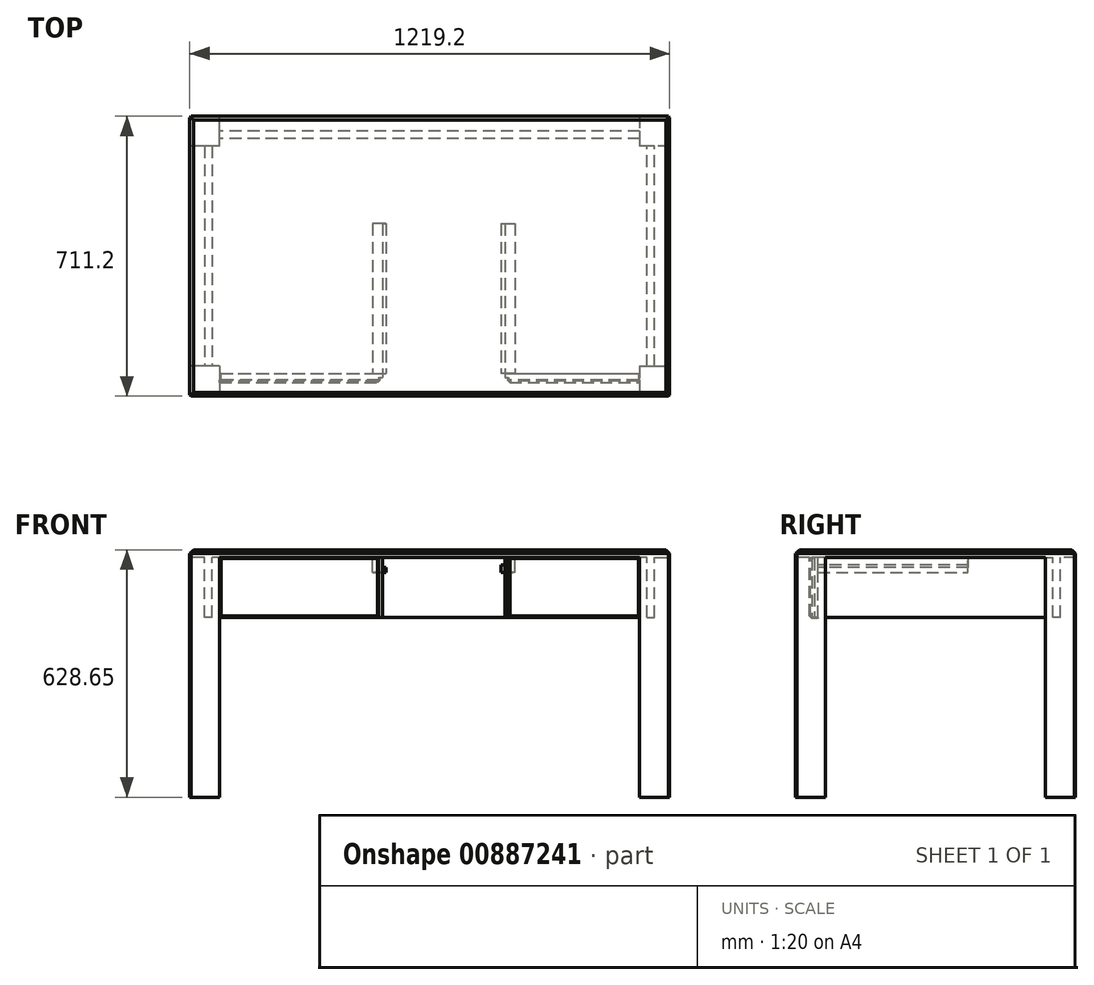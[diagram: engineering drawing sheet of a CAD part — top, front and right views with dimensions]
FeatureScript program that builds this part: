
annotation { "Feature Type Name" : "Feature", "Feature Type Description" : "" }
export const myFeature = defineFeature(function(context is Context, id is Id, definition is map)
    precondition{}
    {
        {
            var Q0;
            Q0=qCreatedBy(makeId("Top.planeOp"),FACE);
            var sketch = newSketch(context, id + "F0", { "sketchPlane" : qUnion([Q0])});
            skLineSegment(sketch, "E0.bottom", {"start": v(609.6, 355.6) * mm, "end": v(-609.6, 355.6) * mm});
            skLineSegment(sketch, "E0.top", {"start": v(609.6, -355.6) * mm, "end": v(-609.6, -355.6) * mm});
            skLineSegment(sketch, "E0.left", {"start": v(609.6, 355.6) * mm, "end": v(609.6, -355.6) * mm});
            skLineSegment(sketch, "E0.right", {"start": v(-609.6, 355.6) * mm, "end": v(-609.6, -355.6) * mm});
            skPoint(sketch, "E0.middle", {"position": v(0, 0) * mm});
            skSolve(sketch);
        }
        {
            var Q0;
            Q0 = qSketchRegion(id + "F0", true);
            extrude(context, id + "F1", {"entities" : qUnion([Q0]), "depth" : 19.05 * mm, "offsetDistance" : 25.4 * mm});
        }
        {
            var Q0;
            Q0=makeQuery(id+"F1.opExtrude","CAP_FACE",FACE,{"disambiguationData":[OSD([sQuery(id+"F0.wireOp",EDGE,"E0.bottom"),sQuery(id+"F0.wireOp",EDGE,"E0.top"),sQuery(id+"F0.wireOp",EDGE,"E0.left"),sQuery(id+"F0.wireOp",EDGE,"E0.right")])],"isStart":true});
            var sketch = newSketch(context, id + "F2", { "sketchPlane" : qUnion([Q0])});
            skLineSegment(sketch, "E1.bottom", {"start": v(-533.4, 279.4) * mm, "end": v(-609.6, 279.4) * mm});
            skLineSegment(sketch, "E1.top", {"start": v(-533.4, 355.6) * mm, "end": v(-609.6, 355.6) * mm});
            skLineSegment(sketch, "E1.left", {"start": v(-533.4, 279.4) * mm, "end": v(-533.4, 355.6) * mm});
            skLineSegment(sketch, "E1.right", {"start": v(-609.6, 279.4) * mm, "end": v(-609.6, 355.6) * mm});
            skSolve(sketch);
        }
        {
            var Q0;
            Q0 = qSketchRegion(id + "F2", true);
            extrude(context, id + "F3", {"entities" : qUnion([Q0]), "operationType" : NewBodyOperationType.ADD, "depth" : 609.6 * mm, "offsetDistance" : 25.4 * mm});
        }
        {
            var Q0;
            Q0=makeQuery(id+"F1.opExtrude","CAP_FACE",FACE,{"disambiguationData":[OSD([sQuery(id+"F0.wireOp",EDGE,"E0.bottom"),sQuery(id+"F0.wireOp",EDGE,"E0.top"),sQuery(id+"F0.wireOp",EDGE,"E0.left"),sQuery(id+"F0.wireOp",EDGE,"E0.right")])],"isStart":true});
            var sketch = newSketch(context, id + "F4", { "sketchPlane" : qUnion([Q0])});
            skLineSegment(sketch, "E2.bottom", {"start": v(533.4, 279.4) * mm, "end": v(609.6, 279.4) * mm});
            skLineSegment(sketch, "E2.top", {"start": v(533.4, 355.6) * mm, "end": v(609.6, 355.6) * mm});
            skLineSegment(sketch, "E2.left", {"start": v(533.4, 279.4) * mm, "end": v(533.4, 355.6) * mm});
            skLineSegment(sketch, "E2.right", {"start": v(609.6, 279.4) * mm, "end": v(609.6, 355.6) * mm});
            skLineSegment(sketch, "E3.bottom", {"start": v(609.6, -355.6) * mm, "end": v(533.4, -355.6) * mm});
            skLineSegment(sketch, "E3.top", {"start": v(609.6, -279.4) * mm, "end": v(533.4, -279.4) * mm});
            skLineSegment(sketch, "E3.left", {"start": v(609.6, -355.6) * mm, "end": v(609.6, -279.4) * mm});
            skLineSegment(sketch, "E3.right", {"start": v(533.4, -355.6) * mm, "end": v(533.4, -279.4) * mm});
            skLineSegment(sketch, "E4.bottom", {"start": v(-533.4, -279.4) * mm, "end": v(-609.6, -279.4) * mm});
            skLineSegment(sketch, "E4.top", {"start": v(-533.4, -355.6) * mm, "end": v(-609.6, -355.6) * mm});
            skLineSegment(sketch, "E4.left", {"start": v(-533.4, -279.4) * mm, "end": v(-533.4, -355.6) * mm});
            skLineSegment(sketch, "E4.right", {"start": v(-609.6, -279.4) * mm, "end": v(-609.6, -355.6) * mm});
            skSolve(sketch);
        }
        {
            var Q0;
            Q0 = qSketchRegion(id + "F4", true);
            extrude(context, id + "F5", {"entities" : qUnion([Q0]), "operationType" : NewBodyOperationType.ADD, "depth" : 609.6 * mm, "offsetDistance" : 25.4 * mm});
        }
        {
            var Q0;
            Q0=makeQuery(id+"F1.opExtrude","CAP_FACE",FACE,{"disambiguationData":[OSD([sQuery(id+"F0.wireOp",EDGE,"E0.bottom"),sQuery(id+"F0.wireOp",EDGE,"E0.top"),sQuery(id+"F0.wireOp",EDGE,"E0.left"),sQuery(id+"F0.wireOp",EDGE,"E0.right")])],"isStart":true});
            var sketch = newSketch(context, id + "F6", { "sketchPlane" : qUnion([Q0])});
            skLineSegment(sketch, "E5", {"start": v(-533.4, 317.5) * mm, "end": v(533.4, 317.5) * mm});
            skLineSegment(sketch, "E6", {"start": v(571.5, 279.4) * mm, "end": v(571.5, -279.4) * mm});
            skLineSegment(sketch, "E7", {"start": v(533.4, -317.5) * mm, "end": v(-533.4, -317.5) * mm});
            skLineSegment(sketch, "E8", {"start": v(-571.5, -279.4) * mm, "end": v(-571.5, 279.4) * mm});
            skLineSegment(sketch, "E9.0", {"start": v(-552.45, -279.4) * mm, "end": v(-552.45, 279.4) * mm});
            skLineSegment(sketch, "E10.0", {"start": v(-533.4, 298.45) * mm, "end": v(533.4, 298.45) * mm});
            skLineSegment(sketch, "E11.0", {"start": v(552.45, 279.4) * mm, "end": v(552.45, -279.4) * mm});
            skLineSegment(sketch, "E12.0", {"start": v(533.4, -298.45) * mm, "end": v(-533.4, -298.45) * mm});
            skSolve(sketch);
        }
        {
            var Q0;
            {var subQ0=sQuery(id+"F6.wireOp",EDGE,"E8");Q0=makeQuery(id+"F6.imprint","IMPRINT",FACE,{"disambiguationData":[TD([[makeQuery(id+"F6.imprint","IMPRINT",EDGE,{"derivedFrom":subQ0}),-1.0]])]});}
            var Q1;
            {var subQ0=sQuery(id+"F6.wireOp",EDGE,"E5");Q1=makeQuery(id+"F6.imprint","IMPRINT",FACE,{"disambiguationData":[TD([[makeQuery(id+"F6.imprint","IMPRINT",EDGE,{"derivedFrom":subQ0}),-1.0]])]});}
            var Q2;
            {var subQ0=sQuery(id+"F6.wireOp",EDGE,"E6");Q2=makeQuery(id+"F6.imprint","IMPRINT",FACE,{"disambiguationData":[TD([[makeQuery(id+"F6.imprint","IMPRINT",EDGE,{"derivedFrom":subQ0}),-1.0]])]});}
            var Q3;
            {var subQ0=sQuery(id+"F6.wireOp",EDGE,"E7");Q3=makeQuery(id+"F6.imprint","IMPRINT",FACE,{"disambiguationData":[TD([[makeQuery(id+"F6.imprint","IMPRINT",EDGE,{"derivedFrom":subQ0}),-1.0]])]});}
            extrude(context, id + "F7", {"entities" : qUnion([Q0, Q1, Q2, Q3]), "operationType" : NewBodyOperationType.ADD, "depth" : 152.4 * mm, "offsetDistance" : 25.4 * mm});
        }
        {
            var Q0;
            Q0=makeQuery(id+"F7.opExtrude","SWEPT_FACE",FACE,{"disambiguationData":[OSD([sQuery(id+"F6.wireOp",EDGE,"E5")])]});
            var sketch = newSketch(context, id + "F8", { "sketchPlane" : qUnion([Q0])});
            skLineSegment(sketch, "E13", {"start": v(-129.98, 0) * mm, "end": v(-129.98, -152.4) * mm});
            skLineSegment(sketch, "E14", {"start": v(-129.98, -152.4) * mm, "end": v(200.22, -152.4) * mm});
            skLineSegment(sketch, "E15", {"start": v(200.22, -152.4) * mm, "end": v(200.22, 0) * mm});
            skLineSegment(sketch, "E16", {"start": v(200.22, 0) * mm, "end": v(-129.98, 0) * mm});
            skLineSegment(sketch, "E17", {"start": v(-120.46, 0) * mm, "end": v(-120.46, -152.4) * mm});
            skLineSegment(sketch, "E18", {"start": v(-120.46, -152.4) * mm, "end": v(190.7, -152.4) * mm});
            skLineSegment(sketch, "E19", {"start": v(190.7, -152.4) * mm, "end": v(190.7, 0) * mm});
            skLineSegment(sketch, "E20", {"start": v(190.7, 0) * mm, "end": v(-120.46, 0) * mm});
            skSolve(sketch);
        }
        {
            var Q0;
            Q0 = qSketchRegion(id + "F8", true);
            extrude(context, id + "F9", {"entities" : qUnion([Q0]), "operationType" : NewBodyOperationType.REMOVE, "oppositeDirection" : true, "depth" : 9.52 * mm, "offsetDistance" : 25.4 * mm});
        }
        {
            var Q0;
            Q0=makeQuery(id+"F8.imprint","IMPRINT",FACE,{"disambiguationData":[TD([[makeQuery(id+"F8.imprint","IMPRINT",EDGE,{"derivedFrom":sQuery(id+"F8.wireOp",EDGE,"E17")}),1.0]])]});
            extrude(context, id + "F10", {"entities" : qUnion([Q0]), "operationType" : NewBodyOperationType.REMOVE, "oppositeDirection" : true, "depth" : 119.56 * mm, "offsetDistance" : 25.4 * mm});
        }
        {
            var Q0;
            {var subQ0=sQuery(id+"F8.wireOp",EDGE,"E20");var subQ2=sQuery(id+"F0.wireOp",EDGE,"E0.top");var subQ4=makeQuery(id+"F1.opExtrude","CAP_FACE",FACE,{"disambiguationData":[OSD([sQuery(id+"F0.wireOp",EDGE,"E0.bottom"),subQ2,sQuery(id+"F0.wireOp",EDGE,"E0.left"),sQuery(id+"F0.wireOp",EDGE,"E0.right")])],"isStart":true});Q0=makeQuery(id+"F10.boolean.opBoolean","MERGE",FACE,{"derivedFrom":[makeQuery(id+"F7.boolean.opBoolean","SPLIT",FACE,{"disambiguationData":[TD([makeQuery(id+"F7.opExtrude","SWEPT_FACE",FACE,{"disambiguationData":[OSD([sQuery(id+"F6.wireOp",EDGE,"E9.0")])]})])],"derivedFrom":subQ4}),makeQuery(id+"F9.boolean.opBoolean","MERGE",FACE,{"derivedFrom":[makeQuery(id+"F7.boolean.opBoolean","SPLIT",FACE,{"disambiguationData":[TD([makeQuery(id+"F1.opExtrude","SWEPT_FACE",FACE,{"disambiguationData":[OSD([subQ2])]})])],"derivedFrom":subQ4})],"fromTools":[makeQuery(id+"F9.opExtrude","SWEPT_FACE",FACE,{"disambiguationData":[OSD([sQuery(id+"F8.wireOp",EDGE,"E16"),subQ0])]})]})],"fromTools":[makeQuery(id+"F10.opExtrude","SWEPT_FACE",FACE,{"disambiguationData":[OSD([subQ0])]})]});}
            var sketch = newSketch(context, id + "F11", { "sketchPlane" : qUnion([Q0])});
            skLineSegment(sketch, "E21", {"start": v(-120.46, 298.45) * mm, "end": v(-120.46, -82.55) * mm});
            skLineSegment(sketch, "E22", {"start": v(-120.46, -82.55) * mm, "end": v(-145.86, -82.55) * mm});
            skLineSegment(sketch, "E23", {"start": v(-145.86, -82.55) * mm, "end": v(-145.86, 298.45) * mm});
            skLineSegment(sketch, "E24", {"start": v(190.7, 298.45) * mm, "end": v(190.7, -82.55) * mm});
            skLineSegment(sketch, "E25", {"start": v(190.7, -82.55) * mm, "end": v(216.1, -82.55) * mm});
            skLineSegment(sketch, "E26", {"start": v(216.1, -82.55) * mm, "end": v(216.1, 298.45) * mm});
            skLineSegment(sketch, "E27", {"start": v(-120.46, 298.45) * mm, "end": v(-110.93, 298.45) * mm});
            skLineSegment(sketch, "E28", {"start": v(-110.93, 298.45) * mm, "end": v(-110.93, -82.55) * mm});
            skLineSegment(sketch, "E29", {"start": v(-110.93, -82.55) * mm, "end": v(-120.46, -82.55) * mm});
            skLineSegment(sketch, "E30", {"start": v(190.7, 298.45) * mm, "end": v(181.17, 298.45) * mm});
            skLineSegment(sketch, "E31", {"start": v(181.17, 298.45) * mm, "end": v(181.17, -82.55) * mm});
            skLineSegment(sketch, "E32", {"start": v(181.17, -82.55) * mm, "end": v(190.7, -82.55) * mm});
            skSolve(sketch);
        }
        {
            var Q0;
            {var subQ0=sQuery(id+"F11.wireOp",EDGE,"E21");Q0=makeQuery(id+"F11.imprint","IMPRINT",FACE,{"disambiguationData":[TD([[makeQuery(id+"F11.imprint","IMPRINT",EDGE,{"derivedFrom":subQ0}),-1.0]])]});}
            var Q1;
            Q1 = qSketchRegion(id + "F11", true);
            var Q2;
            {var subQ0=sQuery(id+"F11.wireOp",EDGE,"E24");Q2=makeQuery(id+"F11.imprint","IMPRINT",FACE,{"disambiguationData":[TD([[makeQuery(id+"F11.imprint","IMPRINT",EDGE,{"derivedFrom":subQ0}),1.0]])]});}
            extrude(context, id + "F12", {"entities" : qUnion([Q0, Q1, Q2]), "operationType" : NewBodyOperationType.ADD, "depth" : 38.1 * mm, "offsetDistance" : 25.4 * mm});
        }
        {
            var Q0;
            Q0=makeQuery(id+"F3.boolean.opBoolean","MERGE",EDGE,{"derivedFrom":[makeQuery(id+"F1.opExtrude","SWEPT_EDGE",EDGE,{"disambiguationData":[OSD([sQuery(id+"F0.wireOp",EDGE,"E0.top"),sQuery(id+"F0.wireOp",EDGE,"E0.right")])]}),makeQuery(id+"F3.opExtrude","SWEPT_EDGE",EDGE,{"disambiguationData":[OSD([sQuery(id+"F2.wireOp",EDGE,"E1.top"),sQuery(id+"F2.wireOp",EDGE,"E1.right")])]})]});
            var Q1;
            Q1=makeQuery(id+"F5.boolean.opBoolean","MERGE",EDGE,{"derivedFrom":[makeQuery(id+"F1.opExtrude","SWEPT_EDGE",EDGE,{"disambiguationData":[OSD([sQuery(id+"F0.wireOp",EDGE,"E0.bottom"),sQuery(id+"F0.wireOp",EDGE,"E0.right")])]}),makeQuery(id+"F5.opExtrude","SWEPT_EDGE",EDGE,{"disambiguationData":[OSD([sQuery(id+"F4.wireOp",EDGE,"E4.top"),sQuery(id+"F4.wireOp",EDGE,"E4.right")])]})]});
            var Q2;
            Q2=makeQuery(id+"F5.boolean.opBoolean","MERGE",EDGE,{"derivedFrom":[makeQuery(id+"F1.opExtrude","SWEPT_EDGE",EDGE,{"disambiguationData":[OSD([sQuery(id+"F0.wireOp",EDGE,"E0.bottom"),sQuery(id+"F0.wireOp",EDGE,"E0.left")])]}),makeQuery(id+"F5.opExtrude","SWEPT_EDGE",EDGE,{"disambiguationData":[OSD([sQuery(id+"F4.wireOp",EDGE,"E3.bottom"),sQuery(id+"F4.wireOp",EDGE,"E3.left")])]})]});
            var Q3;
            Q3=makeQuery(id+"F5.boolean.opBoolean","MERGE",EDGE,{"derivedFrom":[makeQuery(id+"F1.opExtrude","SWEPT_EDGE",EDGE,{"disambiguationData":[OSD([sQuery(id+"F0.wireOp",EDGE,"E0.top"),sQuery(id+"F0.wireOp",EDGE,"E0.left")])]}),makeQuery(id+"F5.opExtrude","SWEPT_EDGE",EDGE,{"disambiguationData":[OSD([sQuery(id+"F4.wireOp",EDGE,"E2.top"),sQuery(id+"F4.wireOp",EDGE,"E2.right")])]})]});
            var Q4;
            {var subQ0=sQuery(id+"F2.wireOp",EDGE,"E1.left");var subQ1=sQuery(id+"F6.wireOp",EDGE,"E5");Q4=makeQuery(id+"F9.boolean.opBoolean","SPLIT",FACE,{"disambiguationData":[TD([makeQuery(id+"F3.opExtrude","SWEPT_FACE",FACE,{"disambiguationData":[OSD([subQ0])]})])],"derivedFrom":makeQuery(id+"F7.opExtrude","SWEPT_FACE",FACE,{"disambiguationData":[OSD([subQ1])]})});}
            var Q5;
            {var subQ0=sQuery(id+"F6.wireOp",EDGE,"E5");var subQ1=sQuery(id+"F4.wireOp",EDGE,"E2.left");Q5=makeQuery(id+"F9.boolean.opBoolean","SPLIT",FACE,{"disambiguationData":[TD([makeQuery(id+"F5.opExtrude","SWEPT_FACE",FACE,{"disambiguationData":[OSD([subQ1])]})])],"derivedFrom":makeQuery(id+"F7.opExtrude","SWEPT_FACE",FACE,{"disambiguationData":[OSD([subQ0])]})});}
            chamfer(context, id + "F13", {"entities" : qUnion([Q0, Q1, Q2, Q3, Q4, Q5]), "width" : 3.17 * mm, "tangentPropagation" : true});
        }
        {
            var Q0;
            Q0=makeQuery(id+"F1.opExtrude","CAP_FACE",FACE,{"disambiguationData":[OSD([sQuery(id+"F0.wireOp",EDGE,"E0.bottom"),sQuery(id+"F0.wireOp",EDGE,"E0.top"),sQuery(id+"F0.wireOp",EDGE,"E0.left"),sQuery(id+"F0.wireOp",EDGE,"E0.right")])],"isStart":false});
            chamfer(context, id + "F14", {"entities" : qUnion([Q0]), "width" : 9.52 * mm, "tangentPropagation" : true});
        }
        {
            var Q0;
            Q0=makeQuery(id+"F12.opExtrude","SWEPT_FACE",FACE,{"disambiguationData":[OSD([sQuery(id+"F6.wireOp",EDGE,"E10.0"),sQuery(id+"F11.wireOp",EDGE,"E30")])]});
            var sketch = newSketch(context, id + "F15", { "sketchPlane" : qUnion([Q0])});
            skLineSegment(sketch, "E33.bottom", {"start": v(190.7, -19.05) * mm, "end": v(181.17, -19.05) * mm});
            skLineSegment(sketch, "E33.top", {"start": v(190.7, 0) * mm, "end": v(181.17, 0) * mm});
            skLineSegment(sketch, "E33.left", {"start": v(190.7, -19.05) * mm, "end": v(190.7, 0) * mm});
            skLineSegment(sketch, "E33.right", {"start": v(181.17, -19.05) * mm, "end": v(181.17, 0) * mm});
            skSolve(sketch);
        }
        {
            var Q0;
            Q0=makeQuery(id+"F15.imprint","IMPRINT",FACE,{"disambiguationData":[TD([[makeQuery(id+"F15.imprint","IMPRINT",EDGE,{"derivedFrom":sQuery(id+"F15.wireOp",EDGE,"E33.bottom")}),-1.0]])]});
            var Q1;
            Q1=makeQuery(id+"F12.opExtrude","SWEPT_FACE",FACE,{"disambiguationData":[OSD([sQuery(id+"F11.wireOp",EDGE,"E25"),sQuery(id+"F11.wireOp",EDGE,"E32")])]});
            extrude(context, id + "F16", {"entities" : qUnion([Q0]), "operationType" : NewBodyOperationType.REMOVE, "endBound" : BoundingType.UP_TO_SURFACE, "oppositeDirection" : true, "depth" : 404.26 * mm, "endBoundEntityFace" : qUnion([Q1]), "offsetDistance" : 25.4 * mm});
        }
        {
            var Q0;
            Q0=makeQuery(id+"F12.opExtrude","SWEPT_FACE",FACE,{"disambiguationData":[OSD([sQuery(id+"F6.wireOp",EDGE,"E10.0"),sQuery(id+"F11.wireOp",EDGE,"E27")])]});
            var sketch = newSketch(context, id + "F17", { "sketchPlane" : qUnion([Q0])});
            skLineSegment(sketch, "E34.bottom", {"start": v(-120.46, 0) * mm, "end": v(-110.93, 0) * mm});
            skLineSegment(sketch, "E34.top", {"start": v(-120.46, -25.4) * mm, "end": v(-110.93, -25.4) * mm});
            skLineSegment(sketch, "E34.left", {"start": v(-120.46, 0) * mm, "end": v(-120.46, -25.4) * mm});
            skLineSegment(sketch, "E34.right", {"start": v(-110.93, 0) * mm, "end": v(-110.93, -25.4) * mm});
            skSolve(sketch);
        }
        {
            var Q0;
            Q0=makeQuery(id+"F17.imprint","IMPRINT",FACE,{"disambiguationData":[TD([[makeQuery(id+"F17.imprint","IMPRINT",EDGE,{"derivedFrom":sQuery(id+"F17.wireOp",EDGE,"E34.bottom")}),-1.0]])]});
            var Q1;
            Q1=makeQuery(id+"F12.opExtrude","SWEPT_FACE",FACE,{"disambiguationData":[OSD([sQuery(id+"F11.wireOp",EDGE,"E22"),sQuery(id+"F11.wireOp",EDGE,"E29")])]});
            extrude(context, id + "F18", {"entities" : qUnion([Q0]), "operationType" : NewBodyOperationType.REMOVE, "endBound" : BoundingType.UP_TO_SURFACE, "oppositeDirection" : true, "depth" : 25.4 * mm, "endBoundEntityFace" : qUnion([Q1]), "offsetDistance" : 25.4 * mm});
        }
    });
